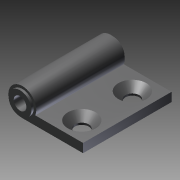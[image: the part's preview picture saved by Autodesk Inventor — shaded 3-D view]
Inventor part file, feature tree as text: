
AUTODESK INVENTOR PART (.ipt)
format: ipt  version: 2011 SP1 (Build 150282100, 282)  size: 125,952 bytes
history: native  units: mm
features: other x35, sketch x5, hole x3, revolve x1, extrude x1
ambient origin geometry x8: Origin, YZ Plane, XZ Plane, XY Plane, X Axis, Y Axis, Z Axis, Center Point
bodies: Solid1 (feature_tree)
feature tree (45):
  revolve  "Revolution1"  [1 undecoded]
  extrude  "Extrusion1"  TaperAngle=0.0deg  [1 undecoded]
  hole  "Hole1"  [1 undecoded]
  hole  "Hole2"  [1 undecoded]
  hole  "Hole3"  [1 undecoded]
  other  "2_XY"
  other  "2_YZ"
  other  "2_ZX"
  other  "2_X"
  other  "2_Y"
  other  "2_Z"
  other  "2_Center"
  other  "to_bolt3_XY"
  other  "to_bolt3_YZ"
  other  "to_bolt3_ZX"
  other  "to_bolt3_X"
  other  "to_bolt3_Y"
  other  "to_bolt3_Z"
  other  "to_bolt3_Center"
  other  "to_bolt3_r_XY"
  other  "to_bolt3_r_YZ"
  other  "to_bolt3_r_ZX"
  other  "to_bolt3_r_X"
  other  "to_bolt3_r_Y"
  other  "to_bolt3_r_Z"
  other  "to_bolt3_r_Center"
  other  "to_bolt4_XY"
  other  "to_bolt4_YZ"
  other  "to_bolt4_ZX"
  other  "to_bolt4_X"
  other  "to_bolt4_Y"
  other  "to_bolt4_Z"
  other  "to_bolt4_Center"
  other  "to_bolt4_r_XY"
  other  "to_bolt4_r_YZ"
  other  "to_bolt4_r_ZX"
  other  "to_bolt4_r_X"
  other  "to_bolt4_r_Y"
  other  "to_bolt4_r_Z"
  other  "to_bolt4_r_Center"
  sketch  "Sketch_1"  dims[d0=360.0deg d1=3.5mm d2=0.0mm]
  sketch  "Sketch_3"  dims[d3=5.5mm d4=6.0mm d5=11.0mm d6=2.0mm d7=90.0deg d8=3.5mm d9=0.0mm]
  sketch  "Sketch3"  dims[d10=5.5mm d11=6.0mm d12=11.0mm d13=2.0mm d14=90.0deg d15=3.5mm d16=0.0mm]
  sketch  "Sketch4"  dims[d17=5.0mm d18=6.0mm d19=4.0mm d20=2.0mm d21=90.0deg d22=36.8mm d23=0.0mm d24=0.0mm d25=0.0mm d26=0.0mm]
  sketch  "Sketch5"
note: 5 required parameter values undecoded (feature->parameter linkage not recoverable at this tier; creation-order binding heuristic only, values carry confidence <= 0.55)